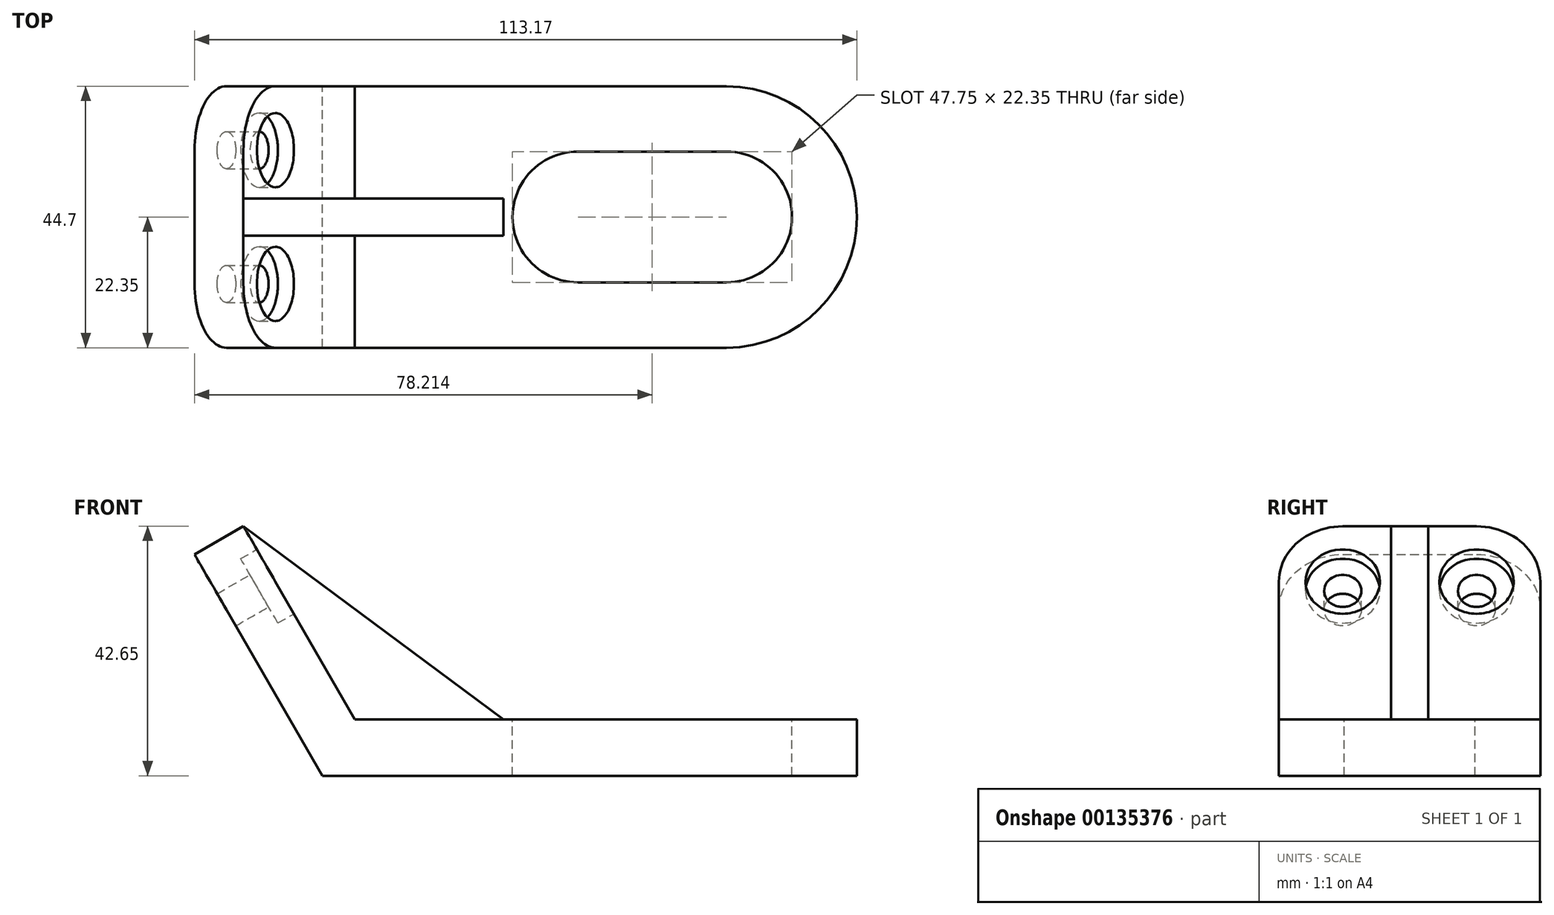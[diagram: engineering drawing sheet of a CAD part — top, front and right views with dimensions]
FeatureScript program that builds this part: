
annotation { "Feature Type Name" : "Feature", "Feature Type Description" : "" }
export const myFeature = defineFeature(function(context is Context, id is Id, definition is map)
    precondition{}
    {
        {
            var Q0;
            Q0=qCreatedBy(makeId("Front.planeOp"),FACE);
            var sketch = newSketch(context, id + "F0", { "sketchPlane" : qUnion([Q0])});
            skLineSegment(sketch, "E0", {"start": v(57.4, 0) * mm, "end": v(-34.03, 0) * mm});
            skLineSegment(sketch, "E1", {"start": v(57.4, 0) * mm, "end": v(57.4, 9.65) * mm});
            skLineSegment(sketch, "E2", {"start": v(57.4, 9.65) * mm, "end": v(-28.46, 9.65) * mm});
            skLineSegment(sketch, "E3", {"start": v(-28.46, 9.65) * mm, "end": v(-47.5, 42.65) * mm});
            skLineSegment(sketch, "E4", {"start": v(-34.03, 0) * mm, "end": v(-55.87, 37.83) * mm});
            skLineSegment(sketch, "E5", {"start": v(-47.5, 42.65) * mm, "end": v(-55.87, 37.83) * mm});
            skLineSegment(sketch, "E6", {"start": v(-47.5, 42.65) * mm, "end": v(-3.06, 9.65) * mm});
            skSolve(sketch);
        }
        {
            var Q0;
            Q0=makeQuery(id+"F0.imprint","IMPRINT",FACE,{"disambiguationData":[TD([[makeQuery(id+"F0.imprint","IMPRINT",EDGE,{"derivedFrom":sQuery(id+"F0.wireOp",EDGE,"E0")}),-1.0]])]});
            extrude(context, id + "F1", {"entities" : qUnion([Q0]), "endBound" : BoundingType.SYMMETRIC, "depth" : 44.7 * mm});
        }
        {
            var Q0;
            {var subQ0=sQuery(id+"F0.wireOp",EDGE,"E3");Q0=makeQuery(id+"F0.imprint","IMPRINT",FACE,{"disambiguationData":[TD([[makeQuery(id+"F0.imprint","IMPRINT",EDGE,{"derivedFrom":subQ0}),-1.0]])]});}
            extrude(context, id + "F2", {"entities" : qUnion([Q0]), "operationType" : NewBodyOperationType.ADD, "endBound" : BoundingType.SYMMETRIC, "depth" : 6.35 * mm});
        }
        {
            var Q0;
            Q0=makeQuery(id+"F1.opExtrude","SWEPT_FACE",FACE,{"disambiguationData":[OSD([sQuery(id+"F0.wireOp",EDGE,"E2")])]});
            var sketch = newSketch(context, id + "F3", { "sketchPlane" : qUnion([Q0])});
            skArc(sketch, "E7", {"start": v(9.64, 11.18) * mm, "mid": v(-1.53, -0.02) * mm, "end": v(9.68, -11.18) * mm});
            skArc(sketch, "E8", {"start": v(35.04, -11.18) * mm, "mid": v(46.22, 0) * mm, "end": v(35.04, 11.18) * mm});
            skLineSegment(sketch, "E9", {"start": v(9.64, 11.18) * mm, "end": v(35.04, 11.18) * mm});
            skLineSegment(sketch, "E10", {"start": v(9.68, -11.18) * mm, "end": v(35.04, -11.18) * mm});
            skArc(sketch, "E11", {"start": v(35.04, -22.35) * mm, "mid": v(57.3, 0) * mm, "end": v(35.04, 22.35) * mm});
            skSolve(sketch);
        }
        {
            var Q0;
            {var subQ0=sQuery(id+"F3.wireOp",EDGE,"E11");Q0=makeQuery(id+"F3.imprint","IMPRINT",FACE,{"disambiguationData":[TD([[makeQuery(id+"F3.imprint","IMPRINT",EDGE,{"derivedFrom":subQ0}),-1.0]])]});}
            var Q1;
            Q1=makeQuery(id+"F3.imprint","IMPRINT",FACE,{"disambiguationData":[TD([[makeQuery(id+"F3.imprint","IMPRINT",EDGE,{"derivedFrom":sQuery(id+"F3.wireOp",EDGE,"E7")}),1.0]])]});
            extrude(context, id + "F4", {"entities" : qUnion([Q0, Q1]), "operationType" : NewBodyOperationType.REMOVE, "oppositeDirection" : true, "depth" : 25.4 * mm});
        }
        {
            var Q0;
            {var subQ1=sQuery(id+"F0.wireOp",EDGE,"E6");var subQ2=sQuery(id+"F0.wireOp",EDGE,"E3");var subQ3=sQuery(id+"F0.wireOp",EDGE,"E2");Q0=makeQuery(id+"F2.boolean.opBoolean","SPLIT",FACE,{"disambiguationData":[TD([makeQuery(id+"F2.opExtrude","CAP_FACE",FACE,{"disambiguationData":[OSD([subQ3,subQ2,subQ1])],"isStart":true})])],"derivedFrom":makeQuery(id+"F1.opExtrude","SWEPT_FACE",FACE,{"disambiguationData":[OSD([subQ2])]})});}
            var sketch = newSketch(context, id + "F5", { "sketchPlane" : qUnion([Q0])});
            skCircle(sketch, "E12", {"center": v(11.43, 49.76) * mm, "radius": 6.35 * mm});
            skCircle(sketch, "E13", {"center": v(-11.43, 49.76) * mm, "radius": 6.35 * mm});
            skCircle(sketch, "E14", {"center": v(-11.43, 49.76) * mm, "radius": 3.18 * mm});
            skCircle(sketch, "E15", {"center": v(11.43, 49.76) * mm, "radius": 3.18 * mm});
            skSolve(sketch);
        }
        {
            var Q0;
            Q0 = qSketchRegion(id + "F5", true);
            extrude(context, id + "F6", {"entities" : qUnion([Q0]), "operationType" : NewBodyOperationType.REMOVE, "oppositeDirection" : true, "depth" : 3.17 * mm});
        }
        {
            var Q0;
            {var subQ0=sQuery(id+"F0.wireOp",EDGE,"E6");var subQ1=sQuery(id+"F0.wireOp",EDGE,"E3");var subQ2=sQuery(id+"F0.wireOp",EDGE,"E2");Q0=makeQuery(id+"F6.boolean.opBoolean","SPLIT",FACE,{"disambiguationData":[TD([makeQuery(id+"F6.opExtrude","SWEPT_FACE",FACE,{"disambiguationData":[OSD([sQuery(id+"F5.wireOp",EDGE,"E14")])]})])],"derivedFrom":makeQuery(id+"F2.boolean.opBoolean","SPLIT",FACE,{"disambiguationData":[TD([makeQuery(id+"F2.opExtrude","CAP_FACE",FACE,{"disambiguationData":[OSD([subQ2,subQ1,subQ0])],"isStart":false})])],"derivedFrom":makeQuery(id+"F1.opExtrude","SWEPT_FACE",FACE,{"disambiguationData":[OSD([subQ1])]})})});}
            var Q1;
            {var subQ1=sQuery(id+"F0.wireOp",EDGE,"E6");var subQ2=sQuery(id+"F0.wireOp",EDGE,"E3");var subQ3=sQuery(id+"F0.wireOp",EDGE,"E2");Q1=makeQuery(id+"F6.boolean.opBoolean","SPLIT",FACE,{"disambiguationData":[TD([makeQuery(id+"F6.opExtrude","SWEPT_FACE",FACE,{"disambiguationData":[OSD([sQuery(id+"F5.wireOp",EDGE,"E15")])]})])],"derivedFrom":makeQuery(id+"F2.boolean.opBoolean","SPLIT",FACE,{"disambiguationData":[TD([makeQuery(id+"F2.opExtrude","CAP_FACE",FACE,{"disambiguationData":[OSD([subQ3,subQ2,subQ1])],"isStart":true})])],"derivedFrom":makeQuery(id+"F1.opExtrude","SWEPT_FACE",FACE,{"disambiguationData":[OSD([subQ2])]})})});}
            extrude(context, id + "F7", {"entities" : qUnion([Q0, Q1]), "operationType" : NewBodyOperationType.REMOVE, "oppositeDirection" : true, "depth" : 25.4 * mm});
        }
        {
            var Q0;
            Q0=makeQuery(id+"F1.opExtrude","CAP_EDGE",EDGE,{"disambiguationData":[OSD([sQuery(id+"F0.wireOp",EDGE,"E5")])],"isStart":false});
            var Q1;
            Q1=makeQuery(id+"F1.opExtrude","CAP_EDGE",EDGE,{"disambiguationData":[OSD([sQuery(id+"F0.wireOp",EDGE,"E5")])],"isStart":true});
            fillet(context, id + "F8", {"entities" : qUnion([Q0, Q1]), "radius" : 10.92 * mm, "tangentPropagation" : true, "allowEdgeOverflow" : false});
        }
    });
